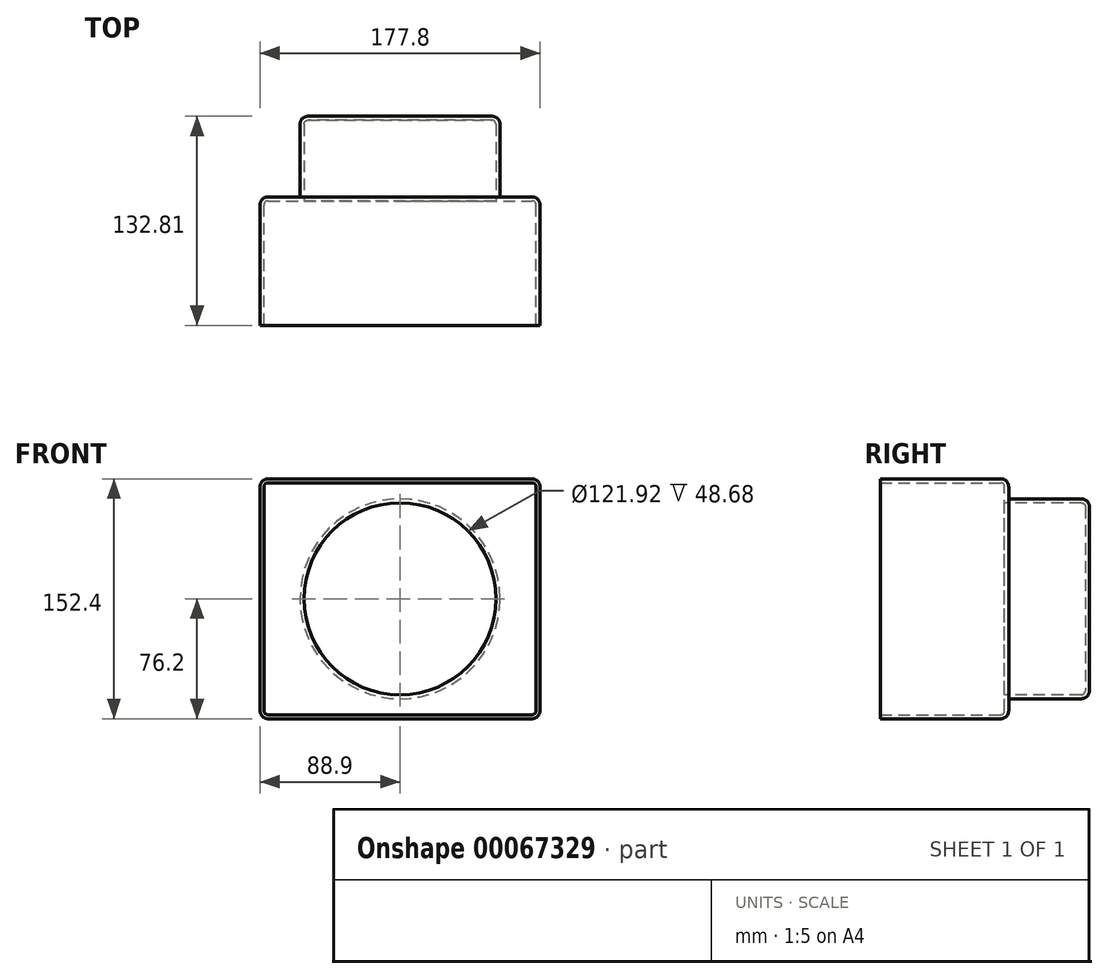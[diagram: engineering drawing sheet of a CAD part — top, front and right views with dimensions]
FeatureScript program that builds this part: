
annotation { "Feature Type Name" : "Feature", "Feature Type Description" : "" }
export const myFeature = defineFeature(function(context is Context, id is Id, definition is map)
    precondition{}
    {
        {
            var Q0;
            Q0=qCreatedBy(makeId("Front.planeOp"),FACE);
            var sketch = newSketch(context, id + "F0", { "sketchPlane" : qUnion([Q0])});
            skLineSegment(sketch, "E0.rect.bottom", {"start": v(88.9, 76.2) * mm, "end": v(-88.9, 76.2) * mm});
            skLineSegment(sketch, "E0.rect.top", {"start": v(88.9, -76.2) * mm, "end": v(-88.9, -76.2) * mm});
            skLineSegment(sketch, "E0.rect.left", {"start": v(88.9, 76.2) * mm, "end": v(88.9, -76.2) * mm});
            skLineSegment(sketch, "E0.rect.right", {"start": v(-88.9, 76.2) * mm, "end": v(-88.9, -76.2) * mm});
            skPoint(sketch, "E0.rect.middle", {"position": v(0, 0) * mm});
            skSolve(sketch);
        }
        {
            var Q0;
            Q0 = qSketchRegion(id + "F0", true);
            extrude(context, id + "F1", {"entities" : qUnion([Q0]), "oppositeDirection" : true, "depth" : 81.6 * mm});
        }
        {
            var Q0;
            Q0=makeQuery(id+"F1.opExtrude","CAP_FACE",FACE,{"disambiguationData":[OSD([sQuery(id+"F0.wireOp",EDGE,"E0.rect.bottom"),sQuery(id+"F0.wireOp",EDGE,"E0.rect.top"),sQuery(id+"F0.wireOp",EDGE,"E0.rect.left"),sQuery(id+"F0.wireOp",EDGE,"E0.rect.right")])],"isStart":false});
            var sketch = newSketch(context, id + "F2", { "sketchPlane" : qUnion([Q0])});
            skCircle(sketch, "E1", {"center": v(0, 0) * mm, "radius": 63.5 * mm});
            skSolve(sketch);
        }
        {
            var Q0;
            Q0 = qSketchRegion(id + "F2", true);
            extrude(context, id + "F3", {"entities" : qUnion([Q0]), "operationType" : NewBodyOperationType.ADD, "depth" : 51.22 * mm});
        }
        {
            var Q0;
            Q0=makeQuery(id+"F3.opExtrude","CAP_EDGE",EDGE,{"disambiguationData":[OSD([sQuery(id+"F2.wireOp",EDGE,"E1")])],"isStart":true});
            var Q1;
            Q1=makeQuery(id+"F3.opExtrude","CAP_EDGE",EDGE,{"disambiguationData":[OSD([sQuery(id+"F2.wireOp",EDGE,"E1")])],"isStart":false});
            var Q2;
            Q2=makeQuery(id+"F1.opExtrude","SWEPT_EDGE",EDGE,{"disambiguationData":[OSD([sQuery(id+"F0.wireOp",EDGE,"E0.rect.bottom"),sQuery(id+"F0.wireOp",EDGE,"E0.rect.right")])]});
            var Q3;
            Q3=makeQuery(id+"F1.opExtrude","SWEPT_EDGE",EDGE,{"disambiguationData":[OSD([sQuery(id+"F0.wireOp",EDGE,"E0.rect.bottom"),sQuery(id+"F0.wireOp",EDGE,"E0.rect.left")])]});
            var Q4;
            Q4=makeQuery(id+"F1.opExtrude","SWEPT_EDGE",EDGE,{"disambiguationData":[OSD([sQuery(id+"F0.wireOp",EDGE,"E0.rect.top"),sQuery(id+"F0.wireOp",EDGE,"E0.rect.right")])]});
            var Q5;
            Q5=makeQuery(id+"F1.opExtrude","SWEPT_EDGE",EDGE,{"disambiguationData":[OSD([sQuery(id+"F0.wireOp",EDGE,"E0.rect.top"),sQuery(id+"F0.wireOp",EDGE,"E0.rect.left")])]});
            fillet(context, id + "F4", {"entities" : qUnion([Q0, Q1, Q2, Q3, Q4, Q5]), "radius" : 5.08 * mm, "tangentPropagation" : true, "allowEdgeOverflow" : false});
        }
        {
            var Q0;
            Q0=makeQuery(id+"F1.opExtrude","CAP_EDGE",EDGE,{"disambiguationData":[OSD([sQuery(id+"F0.wireOp",EDGE,"E0.rect.top")])],"isStart":false});
            fillet(context, id + "F5", {"entities" : qUnion([Q0]), "radius" : 5.08 * mm, "tangentPropagation" : true, "allowEdgeOverflow" : false});
        }
        {
            var Q0;
            Q0=makeQuery(id+"F1.opExtrude","CAP_FACE",FACE,{"disambiguationData":[OSD([sQuery(id+"F0.wireOp",EDGE,"E0.rect.bottom"),sQuery(id+"F0.wireOp",EDGE,"E0.rect.top"),sQuery(id+"F0.wireOp",EDGE,"E0.rect.left"),sQuery(id+"F0.wireOp",EDGE,"E0.rect.right")])],"isStart":true});
            shell(context, id + "F6", {"entities" : qUnion([Q0]), "thickness" : 2.54 * mm});
        }
    });
